# Revit family: ALS.OPL
name_source: partatom
category: Осветительные приборы
revit_build: Autodesk Revit 2016 (Build: 20150220_1215(x64)
units: mm (PartAtom-declared; Revit-internal decimal feet)

## family parameters
Источник света = Да
Общий = Нет
Основа = Грань
При загрузке вырезать с полостями = Нет
Размер круглого соединителя = Использовать диаметр
Тип детали = Нормальный
Точка расчета площади = Нет

## types (1)
- ALS.OPL
    ADSK_Единица измерения = Шт.
    ADSK_Завод-изготовитель = ООО МГК Световые технологии
    ADSK_Код изделия = 1065000090
    ADSK_Количество фаз = 1
    ADSK_Количество фаз числовое = 1
    ADSK_Коэффициент мощности = 0.96
    ADSK_Масса = 2.2
    ADSK_Наименование = Серия светильников с опаловым рассеивателем со степенью защиты IP54 и высокой светоотдачей. Возможно изготовление различных модификаций: с аварийным блоком и управлением освещением, со встроенным датчиком движения. В роли источника света применяются люминесцентные лампы (Т8 или Т5). Предназначены для установки в помещениях с высотой потолков от 2,5 до 4 метров
    ADSK_Напряжение = 230 В
    ADSK_Номинальная мощность = 0 кВт
    ADSK_Полная мощность = 0 кВ·А
    ADSK_Размер_Высота = 95 мм
    ADSK_Размер_Длина = 1270 мм
    ADSK_Размер_Ширина = 106 мм
    ADSK_Ток = 0 А
    ADSK_Энергоэффективность = 59 лм/Вт
    IP Class = IP54
    URL = https://ltcompany.com
    Блок аварийного питания = Нет
    Видимая форма излучения при визуализации = Нет
    Группа модели = Светильники
    Изготовитель = ООО МГК Световые технологии
    Излучение по длине прямоугольника = 1270 мм
    Излучение по ширине прямоугольника = 106 мм
    Класс Защиты = I
    Класс пожароопасности = П-II,IIа
    Климатическая зона = УХЛ2
    Код по классификатору = D5020200
    Корпус = Серый пластик
    Крепление = 5 мм
    Область использования = ЖКХ, Лестницы/коридоры, Медицинские учреждения, Промышленные предприятия, Спортзалы
    Описание = Серия светильников с опаловым рассеивателем со степенью защиты IP54 и высокой светоотдачей. Возможно изготовление различных модификаций: с аварийным блоком и управлением освещением, со встроенным датчиком движения. В роли источника света применяются люминесцентные лампы (Т8 или Т5). Предназначены для установки в помещениях с высотой потолков от 2,5 до 4 метров
    Отметка по умолчанию = 0 мм
    Плафон = Плафон самосвечение
    Подвесы.ширина = 748 мм
    Полная установленная мощность = 0 кВ·А
    Разработчик = ООО ПРОРУБИМ
    Разработчик (телефон) = +7 (495) 649-85-43
    Светофильтр = 16777215
    Смещение цветовой температуры при затухании лампы = <Нет>
    Тип ИС = ЛЛ
    Тип ПРА = ЭПРА
    Тип продукции = Светильник
    Угол наклона = -90.00°
    Файл фотометрической сетки = generic
